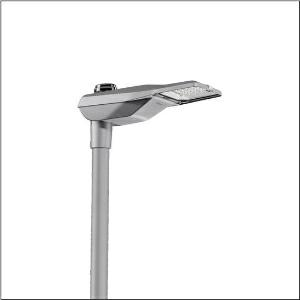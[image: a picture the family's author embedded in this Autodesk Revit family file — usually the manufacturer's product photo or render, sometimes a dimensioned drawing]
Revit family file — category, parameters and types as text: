
# Revit family: streetlight_sl_21_micro___stw1_0a_5xe5e37n08db_8c5c
name_source: partatom
category: Lighting Fixtures
units: mm (PartAtom-declared; Revit-internal decimal feet)

## family parameters
Cut with Voids When Loaded = No
Host = Face
Light Source = No
Part Type = Normal
Room Calculation Point = No
Round Connector Dimension = Use Diameter
Shared = No

## types (1)
- --- (1 x LED, 5110 lm, 39.1 W, 3000K)
    Apparent Load = 39 VA
    CIE Flux Codes = 38 75 98 100 100
    Color Rendering = 70
    Color Temperature = 3000K
    Default Elevation = 1800 mm
    Description = Streetlight SL 21 micro, mast luminaire, primary light control with lens, of PMMA, primary optical cover: cover, of toughened safety glass, transparent, light distribution: STW1.0a, light emission: direct distribution, primary light characteristic: asymmetric, installation type: post-top, LED, 3G 1.5mm², High Power LED, rated luminous flux: 5.110lm, luminous efficacy: 131lm/W, light colour: 730, colour temperature: 3000K, control: overheat protection, pre-setting: linear dimming characteristic, constant luminous flux control, time-dependent luminous flux control, flexible luminous flux parameterisation, mains connection: 230..240V, AC, 50/60Hz, connection cable pre-assembled, cable length: 6,5m, wiring characteristics: H07RN-F, start of lifetime: 39W, end of service life: 41W, reduction: 18W, luminaire housing, of diecast aluminium (EN AC-44300), powder-coated, Siteco® metallic grey (DB 702S), corrosivity category C5 mid according to DIN EN ISO 12944, multi-level sealing system, sealing non-destructively replaceable, inclination adjustable: 0°, 5°, 10°, 15°, length: 528mm, width: 235mm, height: 110mm, spigot size: 76/60mm (post-top), protection rating (complete): IP66, insulation class (complete): insulation class I (protective earthing), certification: CE, ENEC, ENEC+, VDE, impact resistance: IK09, permissible operating ambient temperature for outdoor applications: -40..+50°C, standard-compliant lighting for roads and squares, packaging unit: 1 piece

Light Distribution: STW1.0a
    Height = 110 mm
    Lamp = 1 x LED
    Lamp Light Flux = 5110 lm
    Lamp Power = 39.1 W
    Lamp count = 1
    Length = 528 mm
    Luminous efficacy = 131 lm/W
    Manufacturer = Siteco
    ModVariant = No
    Model = 5XE5E37N08DB
    Number of Poles = 1
    OnlyDefault = Yes
    Power Factor = 1
    Product Name = Streetlight SL 21 micro | STW1.0a
    Product group = mast luminaire | pylon top
    ProductGroupID = 6100
    Protection Class = Protection class I
    Protection Degree = IP 66
    RLX_Detail_Level = 1
    RLX_Emergency_Light_Flux = 0 lm
    RLX_Emergency_Type = 0
    RLX_Emergency_Type_DB = No
    RlxData = <blob elided: 99369 chars, md5=e8872d3d>
    Socket = socket
    Standby Power = 0 W
    System Light Flux = 5110 lm
    System Power = 39 W
    Type Comments = factory setting: luminous flux: 100 % | dim-lin: 254 | 765 mA
    Type Image = l_1294375.jpg
    URL = http://relux.com
    VarID = @adj_105627
    Voltage = 0 V
    Weight = 0.00 kg
    Width = 235 mm

## geometry (parser evidence)
native form markers: Blend x4, Sweep x9
no freeform markers — native parametric forms only
